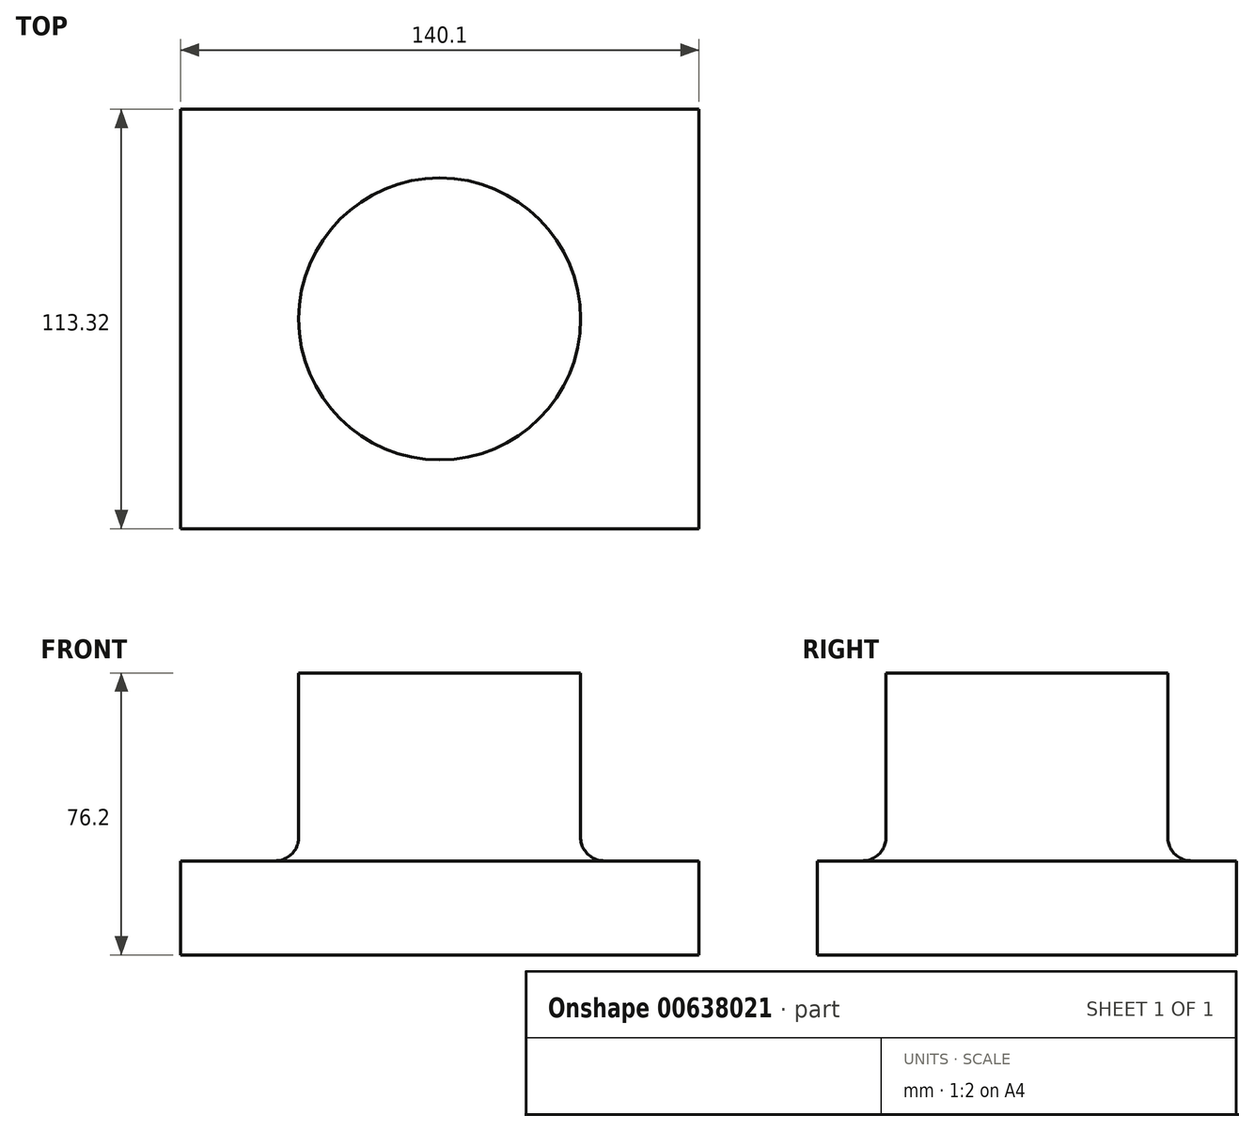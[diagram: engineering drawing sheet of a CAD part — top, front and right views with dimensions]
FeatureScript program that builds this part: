
annotation { "Feature Type Name" : "Feature", "Feature Type Description" : "" }
export const myFeature = defineFeature(function(context is Context, id is Id, definition is map)
    precondition{}
    {
        {
            var Q0;
            Q0=qCreatedBy(makeId("Top.planeOp"),FACE);
            var sketch = newSketch(context, id + "F0", { "sketchPlane" : qUnion([Q0])});
            skCircle(sketch, "E0", {"center": v(0, 0) * mm, "radius": 38.1 * mm});
            skSolve(sketch);
        }
        {
            var Q0;
            Q0=makeQuery(id+"F0.imprint","IMPRINT",FACE,{"disambiguationData":[TD([[makeQuery(id+"F0.imprint","IMPRINT",EDGE,{"derivedFrom":sQuery(id+"F0.wireOp",EDGE,"E0")}),1.0]])]});
            extrude(context, id + "F1", {"entities" : qUnion([Q0]), "depth" : 76.2 * mm, "offsetDistance" : 25.4 * mm});
        }
        {
            var Q0;
            Q0=qCreatedBy(makeId("Top.planeOp"),FACE);
            var sketch = newSketch(context, id + "F2", { "sketchPlane" : qUnion([Q0])});
            skLineSegment(sketch, "E1.bottom", {"start": v(70.05, -56.66) * mm, "end": v(-70.05, -56.66) * mm});
            skLineSegment(sketch, "E1.top", {"start": v(70.05, 56.66) * mm, "end": v(-70.05, 56.66) * mm});
            skLineSegment(sketch, "E1.left", {"start": v(70.05, -56.66) * mm, "end": v(70.05, 56.66) * mm});
            skLineSegment(sketch, "E1.right", {"start": v(-70.05, -56.66) * mm, "end": v(-70.05, 56.66) * mm});
            skPoint(sketch, "E1.middle", {"position": v(0, 0) * mm});
            skSolve(sketch);
        }
        {
            var Q0;
            Q0 = qSketchRegion(id + "F2", true);
            extrude(context, id + "F3", {"entities" : qUnion([Q0]), "operationType" : NewBodyOperationType.ADD, "depth" : 25.4 * mm, "offsetDistance" : 25.4 * mm});
        }
        {
            var Q0;
            Q0=makeQuery(id+"F3.boolean.opBoolean","INTERSECT",EDGE,{"derivedFrom":[makeQuery(id+"F1.opExtrude","SWEPT_FACE",FACE,{"disambiguationData":[OSD([sQuery(id+"F0.wireOp",EDGE,"E0")])]}),makeQuery(id+"F3.opExtrude","CAP_FACE",FACE,{"disambiguationData":[OSD([sQuery(id+"F2.wireOp",EDGE,"E1.bottom"),sQuery(id+"F2.wireOp",EDGE,"E1.top"),sQuery(id+"F2.wireOp",EDGE,"E1.left"),sQuery(id+"F2.wireOp",EDGE,"E1.right")])],"isStart":false})]});
            fillet(context, id + "F4", {"entities" : qUnion([Q0]), "radius" : 6.35 * mm, "tangentPropagation" : true, "allowEdgeOverflow" : false});
        }
    });
